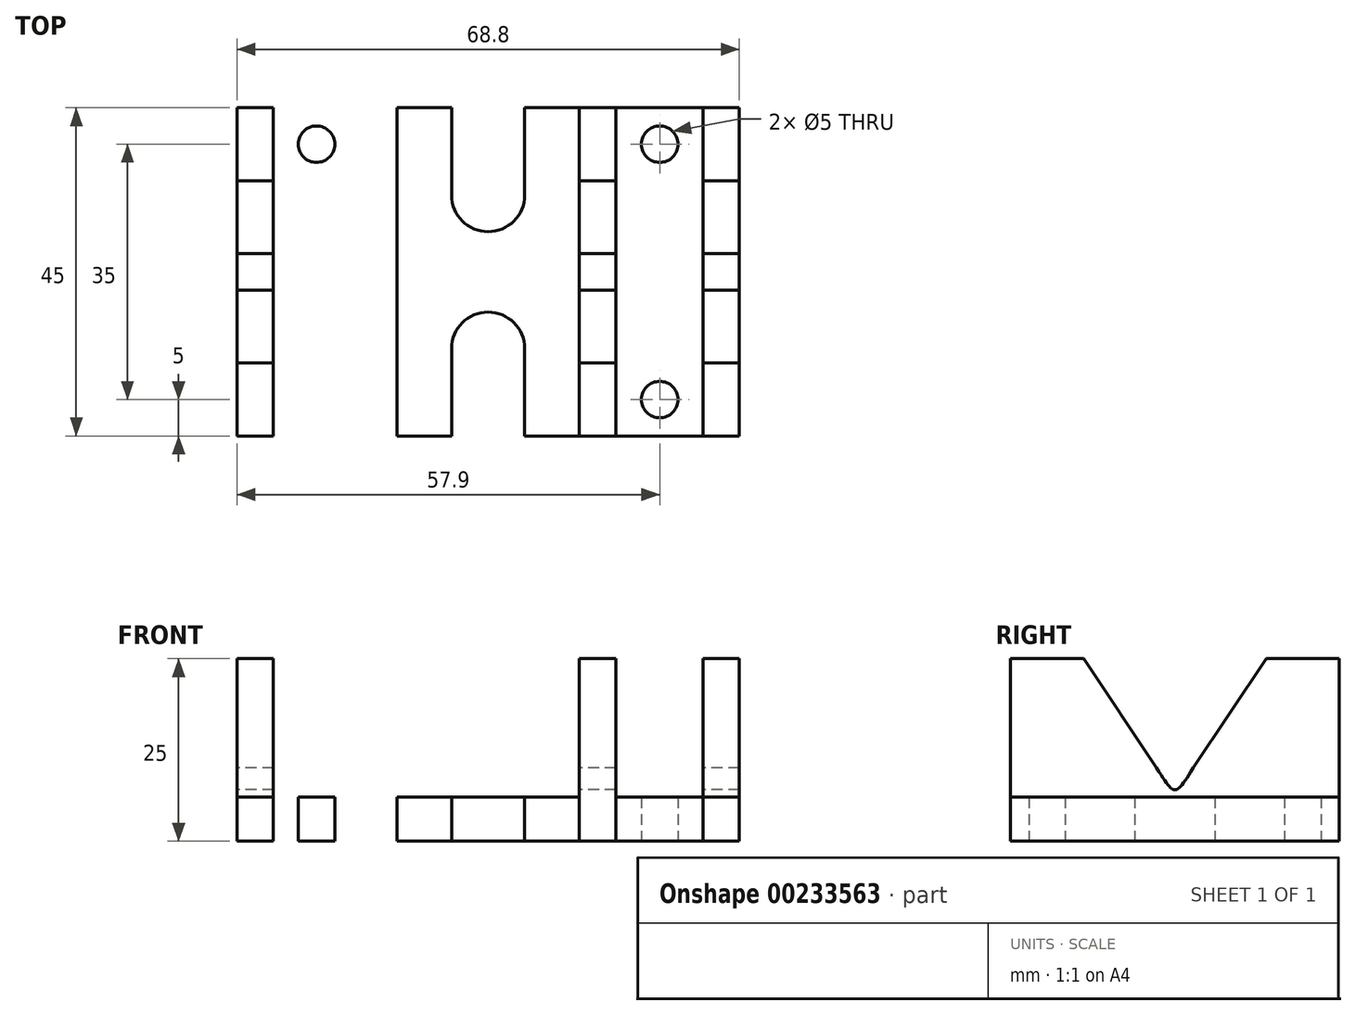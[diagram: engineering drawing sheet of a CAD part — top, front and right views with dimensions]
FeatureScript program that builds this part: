
annotation { "Feature Type Name" : "Feature", "Feature Type Description" : "" }
export const myFeature = defineFeature(function(context is Context, id is Id, definition is map)
    precondition{}
    {
        {
            var Q0;
            Q0=qCreatedBy(makeId("Top.planeOp"),FACE);
            var sketch = newSketch(context, id + "F0", { "sketchPlane" : qUnion([Q0])});
            skLineSegment(sketch, "E0.bottom", {"start": v(34.4, -22.5) * mm, "end": v(-34.4, -22.5) * mm});
            skLineSegment(sketch, "E0.top", {"start": v(34.4, 22.5) * mm, "end": v(-34.4, 22.5) * mm});
            skLineSegment(sketch, "E0.left", {"start": v(34.4, -22.5) * mm, "end": v(34.4, 22.5) * mm});
            skLineSegment(sketch, "E0.right", {"start": v(-34.4, -22.5) * mm, "end": v(-34.4, 22.5) * mm});
            skPoint(sketch, "E0.middle", {"position": v(0, 0) * mm});
            skCircle(sketch, "E1", {"center": v(23.5, 17.5) * mm, "radius": 2.5 * mm});
            skCircle(sketch, "E2.MirrorC", {"center": v(-23.5, 17.5) * mm, "radius": 2.5 * mm});
            skCircle(sketch, "E3.MirrorC", {"center": v(23.5, -17.5) * mm, "radius": 2.5 * mm});
            skCircle(sketch, "E4.MirrorC", {"center": v(-23.5, -17.5) * mm, "radius": 2.5 * mm});
            skCircle(sketch, "E5", {"center": v(0, 10.5) * mm, "radius": 5 * mm});
            skCircle(sketch, "E6.MirrorC", {"center": v(0, -10.5) * mm, "radius": 5 * mm});
            skLineSegment(sketch, "E7", {"start": v(-5, -10.5) * mm, "end": v(-5, -22.5) * mm});
            skLineSegment(sketch, "E8.MirrorCS", {"start": v(5, -10.5) * mm, "end": v(5, -22.5) * mm});
            skLineSegment(sketch, "E9.MirrorCS", {"start": v(-5, 10.5) * mm, "end": v(-5, 22.5) * mm});
            skLineSegment(sketch, "E10.MirrorCS", {"start": v(5, 10.5) * mm, "end": v(5, 22.5) * mm});
            skLineSegment(sketch, "E11.bottom", {"start": v(-17.5, -22.5) * mm, "end": v(-12.5, -22.5) * mm});
            skLineSegment(sketch, "E11.top", {"start": v(-17.5, 22.5) * mm, "end": v(-12.5, 22.5) * mm});
            skLineSegment(sketch, "E11.left", {"start": v(-17.5, -22.5) * mm, "end": v(-17.5, 22.5) * mm});
            skLineSegment(sketch, "E11.right", {"start": v(-12.5, -22.5) * mm, "end": v(-12.5, 22.5) * mm});
            skLineSegment(sketch, "E12.MirrorCS", {"start": v(-29.42, -22.5) * mm, "end": v(-29.42, 22.5) * mm});
            skLineSegment(sketch, "E13.MirrorCS", {"start": v(-34.42, -22.5) * mm, "end": v(-34.42, 22.5) * mm});
            skLineSegment(sketch, "E14.MirrorCS", {"start": v(12.5, -22.5) * mm, "end": v(12.5, 22.5) * mm});
            skLineSegment(sketch, "E15.MirrorCS", {"start": v(17.5, -22.5) * mm, "end": v(17.5, 22.5) * mm});
            skLineSegment(sketch, "E16.MirrorCS", {"start": v(29.42, -22.5) * mm, "end": v(29.42, 22.5) * mm});
            skLineSegment(sketch, "E17.MirrorCS", {"start": v(34.42, -22.5) * mm, "end": v(34.42, 22.5) * mm});
            skSolve(sketch);
        }
        {
            var Q0;
            {var subQ0=sQuery(id+"F0.wireOp",EDGE,"E0.right");Q0=makeQuery(id+"F0.imprint","IMPRINT",FACE,{"disambiguationData":[TD([[makeQuery(id+"F0.imprint","IMPRINT",EDGE,{"derivedFrom":subQ0}),-1.0]])]});}
            var Q1;
            Q1=makeQuery(id+"F0.imprint","IMPRINT",FACE,{"disambiguationData":[TD([[makeQuery(id+"F0.imprint","IMPRINT",EDGE,{"derivedFrom":sQuery(id+"F0.wireOp",EDGE,"E2.MirrorC")}),1.0]])]});
            var Q2;
            {var subQ3=sQuery(id+"F0.wireOp",EDGE,"E7");Q2=makeQuery(id+"F0.imprint","IMPRINT",FACE,{"disambiguationData":[TD([[makeQuery(id+"F0.imprint","IMPRINT",EDGE,{"derivedFrom":subQ3}),-1.0]])]});}
            var Q3;
            Q3=makeQuery(id+"F0.imprint","IMPRINT",FACE,{"disambiguationData":[TD([[makeQuery(id+"F0.imprint","IMPRINT",EDGE,{"derivedFrom":sQuery(id+"F0.wireOp",EDGE,"E1")}),-1.0]])]});
            var Q4;
            {var subQ0=sQuery(id+"F0.wireOp",EDGE,"E0.left");Q4=makeQuery(id+"F0.imprint","IMPRINT",FACE,{"disambiguationData":[TD([[makeQuery(id+"F0.imprint","IMPRINT",EDGE,{"derivedFrom":subQ0}),1.0]])]});}
            extrude(context, id + "F1", {"entities" : qUnion([Q0, Q1, Q2, Q3, Q4]), "depth" : 6 * mm});
        }
        {
            var Q0;
            {var subQ0=sQuery(id+"F0.wireOp",EDGE,"E0.right");Q0=makeQuery(id+"F0.imprint","IMPRINT",FACE,{"disambiguationData":[TD([[makeQuery(id+"F0.imprint","IMPRINT",EDGE,{"derivedFrom":subQ0}),-1.0]])]});}
            var Q1;
            Q1=makeQuery(id+"F0.imprint","IMPRINT",FACE,{"disambiguationData":[TD([[makeQuery(id+"F0.imprint","IMPRINT",EDGE,{"derivedFrom":sQuery(id+"F0.wireOp",EDGE,"E11.bottom")}),1.0]])]});
            var Q2;
            {var subQ0=sQuery(id+"F0.wireOp",EDGE,"E14.MirrorCS");Q2=makeQuery(id+"F0.imprint","IMPRINT",FACE,{"disambiguationData":[TD([[makeQuery(id+"F0.imprint","IMPRINT",EDGE,{"derivedFrom":subQ0}),-1.0]])]});}
            var Q3;
            {var subQ0=sQuery(id+"F0.wireOp",EDGE,"E0.left");Q3=makeQuery(id+"F0.imprint","IMPRINT",FACE,{"disambiguationData":[TD([[makeQuery(id+"F0.imprint","IMPRINT",EDGE,{"derivedFrom":subQ0}),1.0]])]});}
            extrude(context, id + "F2", {"entities" : qUnion([Q0, Q1, Q2, Q3]), "depth" : 25 * mm});
        }
        {
            var Q0;
            Q0=makeQuery(id+"F2.opExtrude","SWEPT_FACE",FACE,{"disambiguationData":[OSD([sQuery(id+"F0.wireOp",EDGE,"E0.right")])]});
            var sketch = newSketch(context, id + "F3", { "sketchPlane" : qUnion([Q0])});
            skLineSegment(sketch, "E18", {"start": v(2.5, 10) * mm, "end": v(12.5, 25) * mm});
            skLineSegment(sketch, "E19", {"start": v(-2.5, 10) * mm, "end": v(-12.5, 25) * mm});
            skFitSpline(sketch, "E20", {"points": [v(-2.5, 10) * mm, v(2.5, 10) * mm], "startDerivative": vector(7.5, -11.94) * mm, "endDerivative": vector(7.5, 11.94) * mm});
            skSolve(sketch);
        }
        {
            var Q0;
            {var subQ0=sQuery(id+"F3.wireOp",EDGE,"E18");Q0=makeQuery(id+"F3.imprint","IMPRINT",FACE,{"disambiguationData":[TD([[makeQuery(id+"F3.imprint","IMPRINT",EDGE,{"derivedFrom":subQ0}),1.0]])]});}
            extrude(context, id + "F4", {"entities" : qUnion([Q0]), "operationType" : NewBodyOperationType.REMOVE, "endBound" : BoundingType.THROUGH_ALL, "oppositeDirection" : true, "depth" : 70 * mm});
        }
    });
